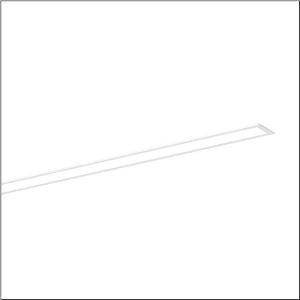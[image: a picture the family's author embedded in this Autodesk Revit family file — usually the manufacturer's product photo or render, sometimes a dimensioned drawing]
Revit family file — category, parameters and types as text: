
# Revit family: silica_21_51mx10tct5w
name_source: partatom
category: Lighting Fixtures
units: mm (PartAtom-declared; Revit-internal decimal feet)

## family parameters
Cut with Voids When Loaded = No
Host = Face
Light Source = No
Part Type = Normal
Room Calculation Point = No
Round Connector Dimension = Use Diameter
Shared = No

## types (1)
- --- (1 x LED, 6000 lm, 51.3 W, 6500K)
    Apparent Load = 51 VA
    CIE Flux Codes = 48 79 96 100 100
    Color Rendering = 80
    Color Temperature = 6500K
    Default Elevation = 1800 mm
    Description = Silica 21, office luminaire, primary optical cover: cover, of PMMA, opal, light emission: direct distribution, primary light characteristic: symmetric, installation type: recessed, LED, rated luminous flux: 6.000lm, luminous efficacy: 112lm/W, light colour: 8tw, colour temperature: 2700..6500K, control gear: DALI DT8, with terminal, 3+2-pole, max. 2.5mm², mains connection: 220..240V, AC, 50/60Hz, rated input power: 53.8W, luminaire housing, of aluminium, traffic white (RAL 9016), length: 3.028mm, width: 79mm, height: 53mm, protection rating (complete): IP20, insulation class (complete): insulation class I (protective earthing), certification: CE, ENEC, VDE, permissible operating ambient temperature: 0..+35°C, standard: EN 50419, packaging unit: 1 piece
    Height = 0 mm  [stored 0 ft]
    Lamp = 1 x LED
    Lamp Light Flux = 6000 lm
    Lamp Power = 51.3 W
    Lamp count = 1
    Length = 3027 mm
    Luminous efficacy = 117 lm/W
    Manufacturer = Siteco
    ModVariant = No
    Model = 51MX10TCT5W
    Mounting Place = Ceiling
    Mounting Type = Recessed
    Number of Poles = 1
    OnlyDefault = Yes
    Power Factor = 1
    Product Name = Silica 21
    Product group = office luminaire | ceiling recessed
    ProductGroupID = 400
    Protection Class = Protection class I
    Protection Degree = IP 20
    RLX_Detail_Level = 1
    RLX_Emergency_Light_Flux = 0 lm
    RLX_Emergency_Type = 0
    RLX_Emergency_Type_DB = No
    RlxData = <blob elided: 17917 chars, md5=0fe01ab9>
    Socket = socket
    Standby Power = 0 W
    System Light Flux = 6000 lm
    System Power = 51 W
    Type Comments = individual setting
    Type Image = l_1335891.jpg
    URL = http://relux.com
    VarID = @adj_140767
    Voltage = 0 V
    Weight = 0.00 kg
    Width = 79 mm

note: [stored X ft] marks values corroborated as IEEE doubles in the binary element streams (Revit-internal decimal feet)

## geometry (parser evidence)
native form markers: Blend x4, Sweep x11
no freeform markers — native parametric forms only
